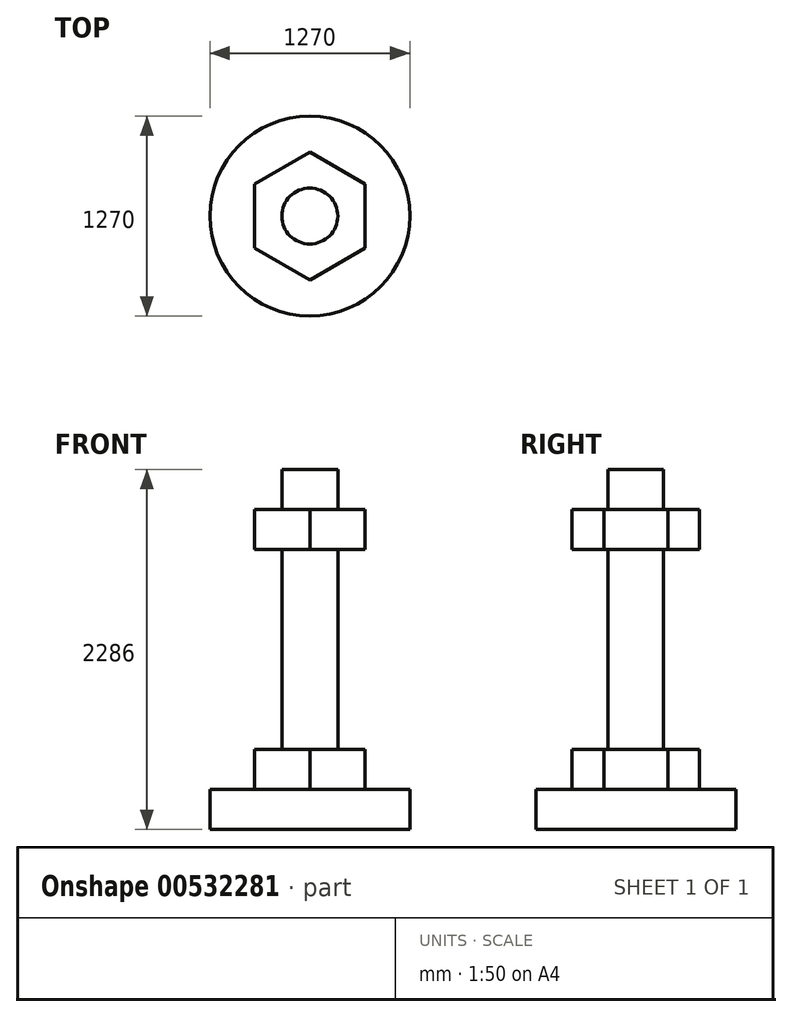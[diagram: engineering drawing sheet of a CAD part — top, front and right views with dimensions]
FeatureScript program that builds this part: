
annotation { "Feature Type Name" : "Feature", "Feature Type Description" : "" }
export const myFeature = defineFeature(function(context is Context, id is Id, definition is map)
    precondition{}
    {
        {
            var Q0;
            Q0=qCreatedBy(makeId("Top.planeOp"),FACE);
            var sketch = newSketch(context, id + "F0", { "sketchPlane" : qUnion([Q0])});
            skCircle(sketch, "E0", {"center": v(0, 0) * mm, "radius": 635 * mm});
            skSolve(sketch);
        }
        {
            var Q0;
            Q0=makeQuery(id+"F0.imprint","IMPRINT",FACE,{"disambiguationData":[TD([[makeQuery(id+"F0.imprint","IMPRINT",EDGE,{"derivedFrom":sQuery(id+"F0.wireOp",EDGE,"E0")}),1.0]])]});
            extrude(context, id + "F1", {"entities" : qUnion([Q0]), "depth" : 254 * mm, "offsetDistance" : 25.4 * mm});
        }
        {
            var Q0;
            Q0=makeQuery(id+"F1.opExtrude","CAP_FACE",FACE,{"disambiguationData":[OSD([sQuery(id+"F0.wireOp",EDGE,"E0")])],"isStart":false});
            var sketch = newSketch(context, id + "F2", { "sketchPlane" : qUnion([Q0])});
            skCircle(sketch, "E1.cCircle", {"center": v(0, 0) * mm, "radius": 351.48 * mm, "construction": true});
            skLineSegment(sketch, "E1.0", {"start": v(351.48, 202.93) * mm, "end": v(351.48, -202.93) * mm});
            skLineSegment(sketch, "E1.1", {"start": v(351.48, -202.93) * mm, "end": v(0, -405.85) * mm});
            skLineSegment(sketch, "E1.2", {"start": v(0, -405.85) * mm, "end": v(-351.48, -202.93) * mm});
            skLineSegment(sketch, "E1.3", {"start": v(-351.48, -202.93) * mm, "end": v(-351.48, 202.93) * mm});
            skLineSegment(sketch, "E1.4", {"start": v(-351.48, 202.93) * mm, "end": v(0, 405.85) * mm});
            skLineSegment(sketch, "E1.5", {"start": v(0, 405.85) * mm, "end": v(351.48, 202.93) * mm});
            skPoint(sketch, "E1.0.midPoint", {"position": v(351.48, 0) * mm});
            skSolve(sketch);
        }
        {
            var Q0;
            Q0 = qSketchRegion(id + "F2", true);
            extrude(context, id + "F3", {"entities" : qUnion([Q0]), "operationType" : NewBodyOperationType.ADD, "depth" : 254 * mm, "offsetDistance" : 25.4 * mm});
        }
        {
            var Q0;
            Q0=makeQuery(id+"F3.opExtrude","CAP_FACE",FACE,{"disambiguationData":[OSD([sQuery(id+"F2.wireOp",EDGE,"E1.0"),sQuery(id+"F2.wireOp",EDGE,"E1.1"),sQuery(id+"F2.wireOp",EDGE,"E1.2"),sQuery(id+"F2.wireOp",EDGE,"E1.3"),sQuery(id+"F2.wireOp",EDGE,"E1.4"),sQuery(id+"F2.wireOp",EDGE,"E1.5")])],"isStart":false});
            var sketch = newSketch(context, id + "F4", { "sketchPlane" : qUnion([Q0])});
            skCircle(sketch, "E2", {"center": v(0, 0) * mm, "radius": 177.53 * mm});
            skSolve(sketch);
        }
        {
            var Q0;
            Q0=makeQuery(id+"F4.imprint","IMPRINT",FACE,{"disambiguationData":[TD([[makeQuery(id+"F4.imprint","IMPRINT",EDGE,{"derivedFrom":sQuery(id+"F4.wireOp",EDGE,"E2")}),1.0]])]});
            extrude(context, id + "F5", {"entities" : qUnion([Q0]), "operationType" : NewBodyOperationType.ADD, "depth" : 1778 * mm, "offsetDistance" : 25.4 * mm});
        }
        {
            var Q0;
            Q0=makeQuery(id+"F3.opExtrude","CAP_FACE",FACE,{"disambiguationData":[OSD([sQuery(id+"F2.wireOp",EDGE,"E1.0"),sQuery(id+"F2.wireOp",EDGE,"E1.1"),sQuery(id+"F2.wireOp",EDGE,"E1.2"),sQuery(id+"F2.wireOp",EDGE,"E1.3"),sQuery(id+"F2.wireOp",EDGE,"E1.4"),sQuery(id+"F2.wireOp",EDGE,"E1.5")])],"isStart":false});
            extrude(context, id + "F6", {"entities" : qUnion([Q0]), "operationType" : NewBodyOperationType.ADD, "depth" : 1524 * mm, "offsetDistance" : 25.4 * mm, "hasSecondDirection" : true, "secondDirectionOppositeDirection" : false, "secondDirectionDepth" : 1270 * mm});
        }
    });
